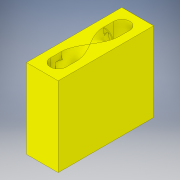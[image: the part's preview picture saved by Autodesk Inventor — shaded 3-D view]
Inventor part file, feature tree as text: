
AUTODESK INVENTOR PART (.ipt)
format: ipt  version: 2019 (Build 230136000, 136)  size: 243,712 bytes
history: native  units: mm
features: sketch x5, extrude x3, sweep x1
ambient origin geometry x8: Origin, YZ Plane, XZ Plane, XY Plane, X Axis, Y Axis, Z Axis, Center Point
bodies: Solid1 (feature_tree)
feature tree (9):
  extrude  "Extrusion1"  Depth=30.0mm
  sweep  "Sweep1"
  extrude  "Extrusion2"  Depth=10.0mm
  extrude  "Extrusion3"  TaperAngle=0.0deg  [1 undecoded]
  sketch  "Sketch1"  dims[d0=10.0mm d1=30.0mm]
  sketch  "Sketch2"  dims[d2=5.0mm d4=20.0mm]
  sketch  "Sketch3"  dims[d5=25.0mm d6=0.0mm d7=10.0mm]
  sketch  "Sketch4"  dims[d8=7.5mm d9=0.0mm d10=0.0mm]
  sketch  "Sketch5"  dims[d11=2.0mm d12=0.0mm d13=3.0mm d14=0.0mm]
note: 1 required parameter value undecoded (feature->parameter linkage not recoverable at this tier; creation-order binding heuristic only, values carry confidence <= 0.55)
